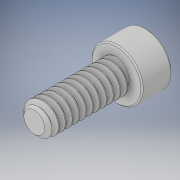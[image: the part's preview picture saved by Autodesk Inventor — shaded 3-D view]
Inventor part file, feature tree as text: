
AUTODESK INVENTOR PART (.ipt)
format: ipt  version: 2018 (Build 220112000, 112)  size: 688,128 bytes
history: native  units: in
note: dims shown in document units (in); Inventor stores cm internally (conversion verified against a paired STEP export)
features: chamfer x1
ambient origin geometry x8: Origin, YZ Plane, XZ Plane, XY Plane, X Axis, Y Axis, Z Axis, Center Point
bodies: Solid1 (feature_tree)
feature tree (1):
  chamfer  "Chamfer2"  [1 undecoded]
note: 1 required parameter value undecoded (feature->parameter linkage not recoverable at this tier; creation-order binding heuristic only, values carry confidence <= 0.55)
